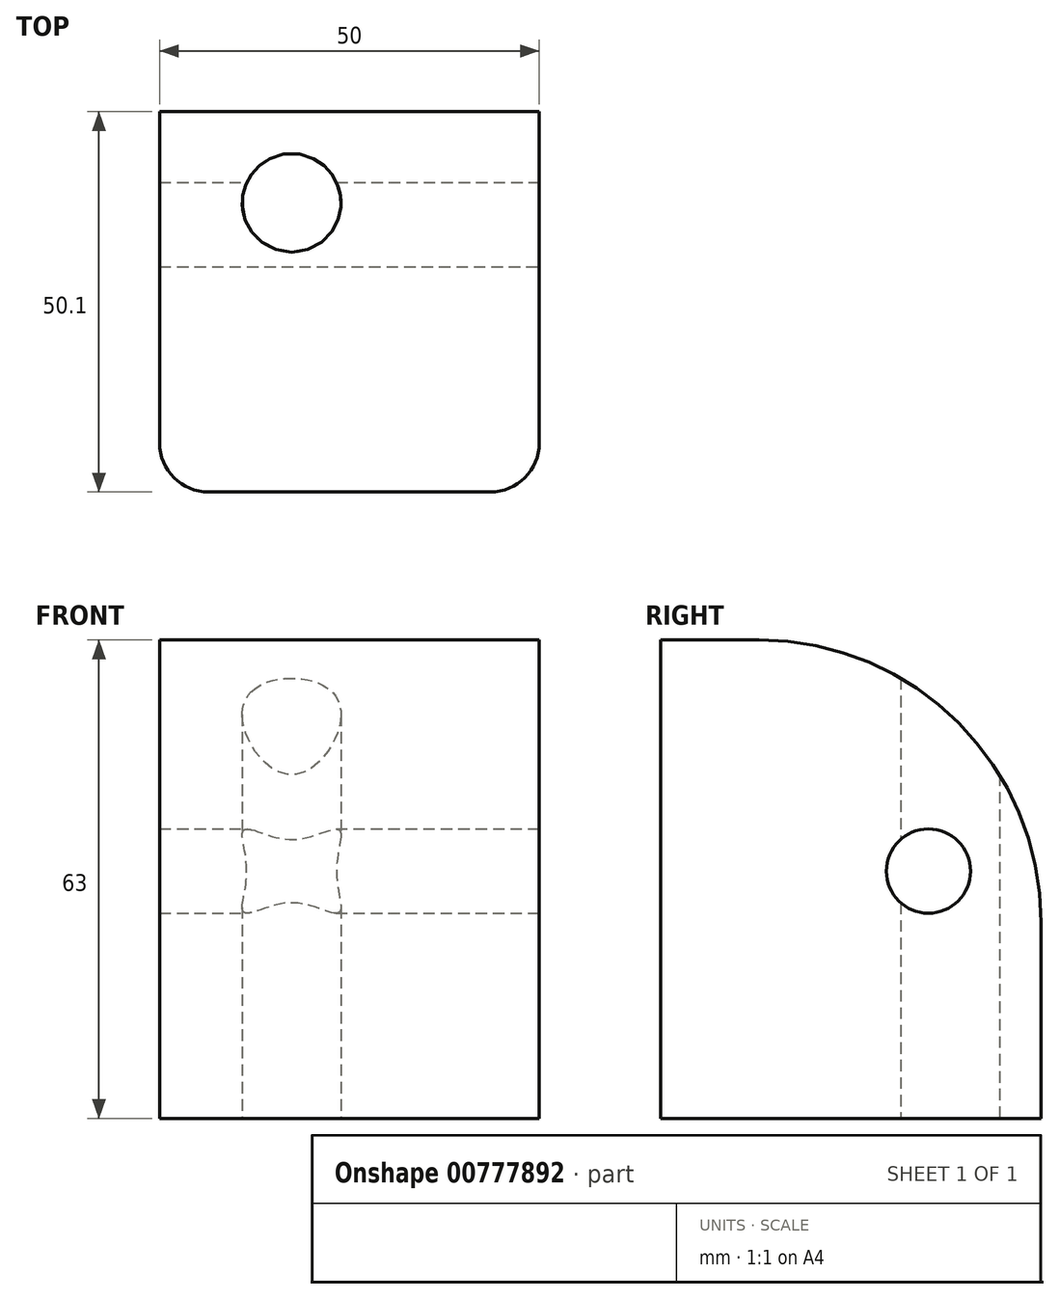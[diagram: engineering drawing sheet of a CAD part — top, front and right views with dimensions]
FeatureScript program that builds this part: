
annotation { "Feature Type Name" : "Feature", "Feature Type Description" : "" }
export const myFeature = defineFeature(function(context is Context, id is Id, definition is map)
    precondition{}
    {
        {
            var Q0;
            Q0=qCreatedBy(makeId("Top.planeOp"),FACE);
            var sketch = newSketch(context, id + "F0", { "sketchPlane" : qUnion([Q0])});
            skLineSegment(sketch, "E0.bottom", {"start": v(-18.53, -25.05) * mm, "end": v(18.53, -25.05) * mm});
            skLineSegment(sketch, "E0.top", {"start": v(-25, 25.05) * mm, "end": v(25, 25.05) * mm});
            skLineSegment(sketch, "E0.left", {"start": v(-25, -18.58) * mm, "end": v(-25, 25.05) * mm});
            skLineSegment(sketch, "E0.right", {"start": v(25, -18.58) * mm, "end": v(25, 25.05) * mm});
            skPoint(sketch, "E0.middle", {"position": v(0, 0) * mm});
            skCircle(sketch, "E1", {"center": v(-7.62, 13.05) * mm, "radius": 6.5 * mm});
            skLineSegment(sketch, "E2", {"start": v(-25, 25.05) * mm, "end": v(25, 10.05) * mm, "construction": true});
            skLineSegment(sketch, "E3", {"start": v(-7.62, 13.05) * mm, "end": v(-25, 13.05) * mm, "construction": true});
            skPoint(sketch, "E4.visualSharp", {"position": v(-25, -25.05) * mm});
            skArc(sketch, "E4.filletArc", {"start": v(-25, -18.58) * mm, "mid": v(-23.1, -23.15) * mm, "end": v(-18.53, -25.05) * mm});
            skPoint(sketch, "E5.visualSharp", {"position": v(25, -25.05) * mm});
            skArc(sketch, "E5.filletArc", {"start": v(18.53, -25.05) * mm, "mid": v(23.1, -23.15) * mm, "end": v(25, -18.58) * mm});
            skSolve(sketch);
        }
        {
            var Q0;
            Q0=makeQuery(id+"F0.imprint","IMPRINT",FACE,{"disambiguationData":[TD([[makeQuery(id+"F0.imprint","IMPRINT",EDGE,{"derivedFrom":sQuery(id+"F0.wireOp",EDGE,"E0.bottom")}),1.0]])]});
            extrude(context, id + "F1", {"entities" : qUnion([Q0]), "depth" : 63 * mm, "offsetDistance" : 25 * mm});
        }
        {
            var Q0;
            Q0=makeQuery(id+"F1.opExtrude","CAP_EDGE",EDGE,{"disambiguationData":[OSD([sQuery(id+"F0.wireOp",EDGE,"E0.top")])],"isStart":false});
            fillet(context, id + "F2", {"entities" : qUnion([Q0]), "radius" : 37.18 * mm, "tangentPropagation" : true, "allowEdgeOverflow" : false});
        }
        {
            var Q0;
            Q0=makeQuery(id+"F1.opExtrude","SWEPT_FACE",FACE,{"disambiguationData":[OSD([sQuery(id+"F0.wireOp",EDGE,"E0.right")])]});
            var sketch = newSketch(context, id + "F3", { "sketchPlane" : qUnion([Q0])});
            skCircle(sketch, "E6", {"center": v(10.2, 32.56) * mm, "radius": 5.54 * mm});
            skSolve(sketch);
        }
        {
            var Q0;
            Q0 = qSketchRegion(id + "F3", true);
            extrude(context, id + "F4", {"entities" : qUnion([Q0]), "operationType" : NewBodyOperationType.REMOVE, "endBound" : BoundingType.THROUGH_ALL, "oppositeDirection" : true, "depth" : 25 * mm, "offsetDistance" : 25 * mm});
        }
    });
